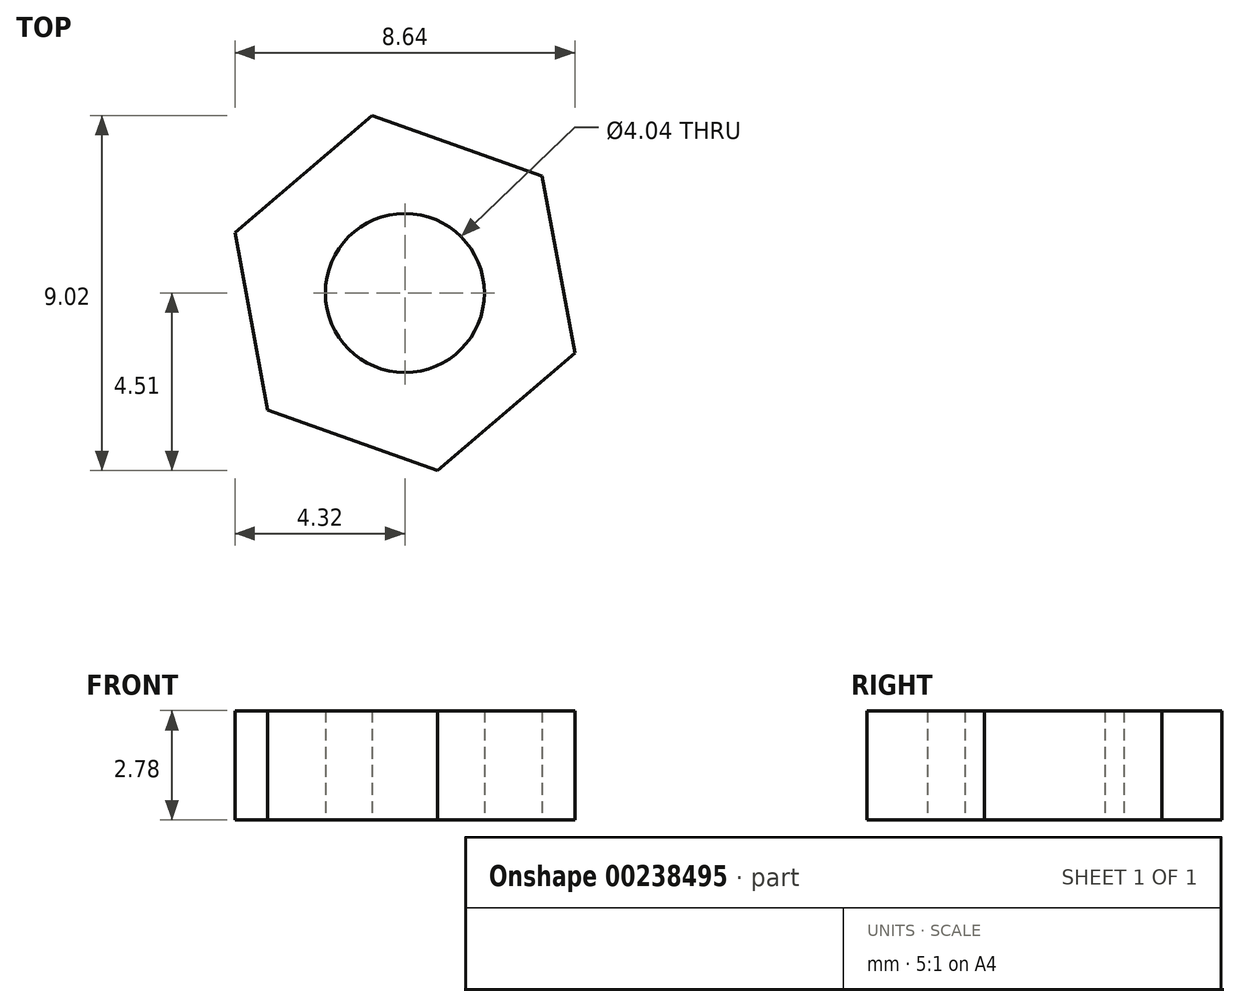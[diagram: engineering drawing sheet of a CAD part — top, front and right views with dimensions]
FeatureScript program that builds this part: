
annotation { "Feature Type Name" : "Feature", "Feature Type Description" : "" }
export const myFeature = defineFeature(function(context is Context, id is Id, definition is map)
    precondition{}
    {
        {
            var Q0;
            Q0=qCreatedBy(makeId("Top.planeOp"),FACE);
            var sketch = newSketch(context, id + "F0", { "sketchPlane" : qUnion([Q0])});
            skCircle(sketch, "E0.cCircle", {"center": v(0, 0) * mm, "radius": 3.97 * mm, "construction": true});
            skLineSegment(sketch, "E0.0", {"start": v(-0.84, 4.5) * mm, "end": v(3.48, 2.98) * mm});
            skLineSegment(sketch, "E0.1", {"start": v(3.48, 2.98) * mm, "end": v(4.32, -1.53) * mm});
            skLineSegment(sketch, "E0.2", {"start": v(4.32, -1.53) * mm, "end": v(0.84, -4.5) * mm});
            skLineSegment(sketch, "E0.3", {"start": v(0.84, -4.5) * mm, "end": v(-3.48, -2.98) * mm});
            skLineSegment(sketch, "E0.4", {"start": v(-3.48, -2.98) * mm, "end": v(-4.32, 1.53) * mm});
            skLineSegment(sketch, "E0.5", {"start": v(-4.32, 1.53) * mm, "end": v(-0.84, 4.5) * mm});
            skPoint(sketch, "E0.0.midPoint", {"position": v(1.32, 3.74) * mm});
            skCircle(sketch, "E1", {"center": v(0, 0) * mm, "radius": 2.02 * mm});
            skSolve(sketch);
        }
        {
            var Q0;
            Q0 = qSketchRegion(id + "F0", true);
            extrude(context, id + "F1", {"entities" : qUnion([Q0]), "depth" : 2.78 * mm});
        }
    });
